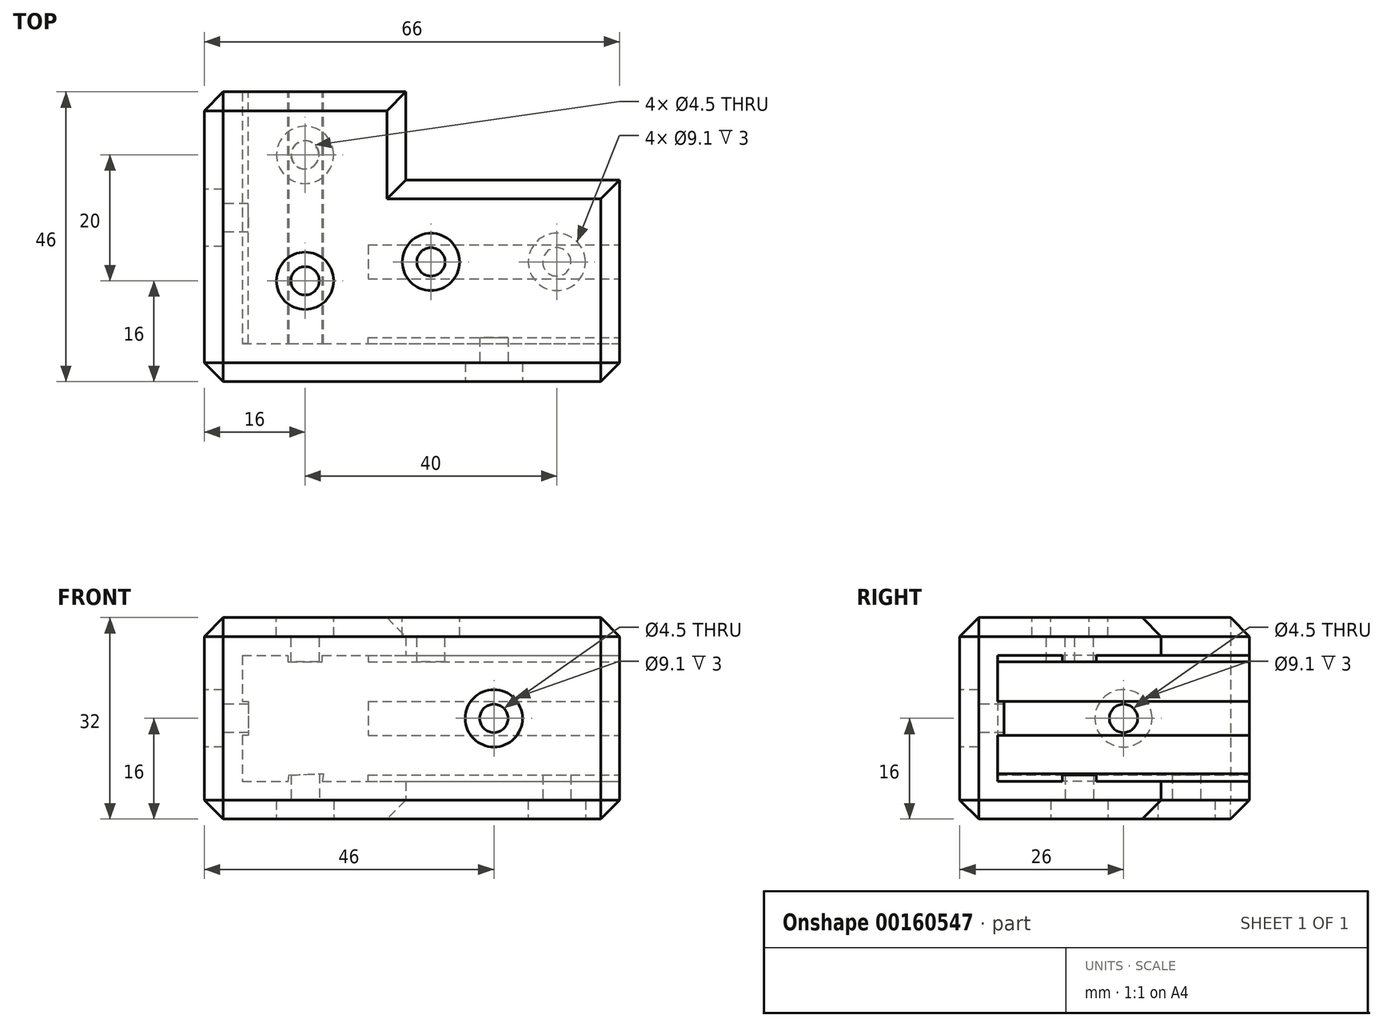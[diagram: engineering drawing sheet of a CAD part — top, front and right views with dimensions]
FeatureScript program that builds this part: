
annotation { "Feature Type Name" : "Feature", "Feature Type Description" : "" }
export const myFeature = defineFeature(function(context is Context, id is Id, definition is map)
    precondition{}
    {
        {
            var Q0;
            Q0=qCreatedBy(makeId("Top.planeOp"),FACE);
            var sketch = newSketch(context, id + "F0", { "sketchPlane" : qUnion([Q0])});
            skLineSegment(sketch, "E0", {"start": v(20, 40) * mm, "end": v(20, 20) * mm, "construction": true});
            skLineSegment(sketch, "E1", {"start": v(20, 20) * mm, "end": v(60, 20) * mm, "construction": true});
            skLineSegment(sketch, "E2", {"start": v(60, 20) * mm, "end": v(60, 0) * mm, "construction": true});
            skLineSegment(sketch, "E3", {"start": v(60, 0) * mm, "end": v(0, 0) * mm, "construction": true});
            skLineSegment(sketch, "E4", {"start": v(0, 0) * mm, "end": v(0, 40) * mm, "construction": true});
            skLineSegment(sketch, "E5", {"start": v(0, 40) * mm, "end": v(20, 40) * mm, "construction": true});
            skLineSegment(sketch, "E6", {"start": v(3.86, 40) * mm, "end": v(26, 40) * mm});
            skLineSegment(sketch, "E7", {"start": v(26, 40) * mm, "end": v(26, 26) * mm});
            skLineSegment(sketch, "E8", {"start": v(26, 26) * mm, "end": v(60, 26) * mm});
            skLineSegment(sketch, "E9", {"start": v(60, 26) * mm, "end": v(60, -6) * mm});
            skLineSegment(sketch, "E10", {"start": v(60, -6) * mm, "end": v(-6, -6) * mm});
            skLineSegment(sketch, "E11", {"start": v(-6, -6) * mm, "end": v(-6, 40) * mm});
            skLineSegment(sketch, "E12", {"start": v(-6, 40) * mm, "end": v(3.86, 40) * mm});
            skSolve(sketch);
        }
        {
            var Q0;
            Q0 = qSketchRegion(id + "F0", true);
            extrude(context, id + "F1", {"entities" : qUnion([Q0]), "depth" : 6 * mm});
        }
        {
            var Q0;
            Q0=makeQuery(id+"F1.opExtrude","CAP_FACE",FACE,{"disambiguationData":[OSD([sQuery(id+"F0.wireOp",EDGE,"E6"),sQuery(id+"F0.wireOp",EDGE,"E7"),sQuery(id+"F0.wireOp",EDGE,"E8"),sQuery(id+"F0.wireOp",EDGE,"E9"),sQuery(id+"F0.wireOp",EDGE,"E10"),sQuery(id+"F0.wireOp",EDGE,"E11"),sQuery(id+"F0.wireOp",EDGE,"E12")])],"isStart":false});
            var sketch = newSketch(context, id + "F2", { "sketchPlane" : qUnion([Q0])});
            skLineSegment(sketch, "E13", {"start": v(-6, 40) * mm, "end": v(0, 40) * mm});
            skLineSegment(sketch, "E14", {"start": v(0, 40) * mm, "end": v(0, 0) * mm});
            skLineSegment(sketch, "E15", {"start": v(0, 0) * mm, "end": v(60, 0) * mm});
            skLineSegment(sketch, "E16", {"start": v(60, 0) * mm, "end": v(60, -6) * mm});
            skLineSegment(sketch, "E17", {"start": v(60, -6) * mm, "end": v(-6, -6) * mm});
            skLineSegment(sketch, "E18", {"start": v(-6, -6) * mm, "end": v(-6, 40) * mm});
            skSolve(sketch);
        }
        {
            var Q0;
            Q0 = qSketchRegion(id + "F2", true);
            extrude(context, id + "F3", {"entities" : qUnion([Q0]), "operationType" : NewBodyOperationType.ADD, "depth" : 20 * mm});
        }
        {
            var Q0;
            Q0=makeQuery(id+"F3.opExtrude","CAP_FACE",FACE,{"disambiguationData":[OSD([sQuery(id+"F2.wireOp",EDGE,"E13"),sQuery(id+"F2.wireOp",EDGE,"E14"),sQuery(id+"F2.wireOp",EDGE,"E15"),sQuery(id+"F2.wireOp",EDGE,"E16"),sQuery(id+"F2.wireOp",EDGE,"E17"),sQuery(id+"F2.wireOp",EDGE,"E18")])],"isStart":false});
            var sketch = newSketch(context, id + "F4", { "sketchPlane" : qUnion([Q0])});
            skLineSegment(sketch, "E19", {"start": v(-6, -6) * mm, "end": v(-6, 40) * mm});
            skLineSegment(sketch, "E20", {"start": v(-6, 40) * mm, "end": v(26, 40) * mm});
            skLineSegment(sketch, "E21", {"start": v(26, 40) * mm, "end": v(26, 26) * mm});
            skLineSegment(sketch, "E22", {"start": v(26, 26) * mm, "end": v(60, 26) * mm});
            skLineSegment(sketch, "E23", {"start": v(60, 26) * mm, "end": v(60, -6) * mm});
            skLineSegment(sketch, "E24", {"start": v(60, -6) * mm, "end": v(-6, -6) * mm});
            skSolve(sketch);
        }
        {
            var Q0;
            Q0 = qSketchRegion(id + "F4", true);
            extrude(context, id + "F5", {"entities" : qUnion([Q0]), "operationType" : NewBodyOperationType.ADD, "depth" : 6 * mm});
        }
        {
            var Q0;
            Q0=makeQuery(id+"F5.boolean.opBoolean","MERGE",FACE,{"derivedFrom":[makeQuery(id+"F3.boolean.opBoolean","MERGE",FACE,{"derivedFrom":[makeQuery(id+"F1.opExtrude","SWEPT_FACE",FACE,{"disambiguationData":[OSD([sQuery(id+"F0.wireOp",EDGE,"E9")])]}),makeQuery(id+"F3.opExtrude","SWEPT_FACE",FACE,{"disambiguationData":[OSD([sQuery(id+"F2.wireOp",EDGE,"E16")])]})]}),makeQuery(id+"F5.opExtrude","SWEPT_FACE",FACE,{"disambiguationData":[OSD([sQuery(id+"F4.wireOp",EDGE,"E23")])]})]});
            var sketch = newSketch(context, id + "F6", { "sketchPlane" : qUnion([Q0])});
            skLineSegment(sketch, "E25", {"start": v(13, 26) * mm, "end": v(10.29, 26) * mm});
            skLineSegment(sketch, "E26", {"start": v(10.29, 26) * mm, "end": v(10.29, 25) * mm});
            skLineSegment(sketch, "E27", {"start": v(10.29, 25) * mm, "end": v(15.7, 25) * mm});
            skLineSegment(sketch, "E28", {"start": v(15.7, 25) * mm, "end": v(15.7, 26) * mm});
            skLineSegment(sketch, "E29", {"start": v(15.7, 26) * mm, "end": v(13, 26) * mm});
            skLineSegment(sketch, "E30", {"start": v(13, 6) * mm, "end": v(10.29, 6) * mm});
            skLineSegment(sketch, "E31", {"start": v(10.29, 6) * mm, "end": v(10.29, 7) * mm});
            skLineSegment(sketch, "E32", {"start": v(10.29, 7) * mm, "end": v(15.7, 7) * mm});
            skLineSegment(sketch, "E33", {"start": v(15.7, 7) * mm, "end": v(15.7, 6) * mm});
            skLineSegment(sketch, "E34", {"start": v(15.7, 6) * mm, "end": v(13, 6) * mm});
            skLineSegment(sketch, "E35", {"start": v(0, 16) * mm, "end": v(0, 18.7) * mm});
            skLineSegment(sketch, "E36", {"start": v(0, 18.7) * mm, "end": v(1, 18.7) * mm});
            skLineSegment(sketch, "E37", {"start": v(1, 18.7) * mm, "end": v(1, 13.29) * mm});
            skLineSegment(sketch, "E38", {"start": v(1, 13.29) * mm, "end": v(0, 13.29) * mm});
            skLineSegment(sketch, "E39", {"start": v(0, 13.29) * mm, "end": v(0, 16) * mm});
            skSolve(sketch);
        }
        {
            var Q0;
            Q0 = qSketchRegion(id + "F6", true);
            extrude(context, id + "F7", {"entities" : qUnion([Q0]), "operationType" : NewBodyOperationType.ADD, "oppositeDirection" : true, "depth" : 40 * mm});
        }
        {
            var Q0;
            Q0=makeQuery(id+"F5.boolean.opBoolean","MERGE",FACE,{"derivedFrom":[makeQuery(id+"F3.boolean.opBoolean","MERGE",FACE,{"derivedFrom":[makeQuery(id+"F1.opExtrude","SWEPT_FACE",FACE,{"disambiguationData":[OSD([sQuery(id+"F0.wireOp",EDGE,"E6"),sQuery(id+"F0.wireOp",EDGE,"E12")])]}),makeQuery(id+"F3.opExtrude","SWEPT_FACE",FACE,{"disambiguationData":[OSD([sQuery(id+"F2.wireOp",EDGE,"E13")])]})]}),makeQuery(id+"F5.opExtrude","SWEPT_FACE",FACE,{"disambiguationData":[OSD([sQuery(id+"F4.wireOp",EDGE,"E20")])]})]});
            var sketch = newSketch(context, id + "F8", { "sketchPlane" : qUnion([Q0])});
            skLineSegment(sketch, "E40", {"start": v(0, 16) * mm, "end": v(0, 18.71) * mm});
            skLineSegment(sketch, "E41", {"start": v(0, 18.71) * mm, "end": v(-1, 18.71) * mm});
            skLineSegment(sketch, "E42", {"start": v(-1, 18.7) * mm, "end": v(-1, 13.29) * mm});
            skLineSegment(sketch, "E43", {"start": v(-1, 13.29) * mm, "end": v(0, 13.29) * mm});
            skLineSegment(sketch, "E44", {"start": v(0, 13.29) * mm, "end": v(0, 16) * mm});
            skLineSegment(sketch, "E45", {"start": v(-10, 26) * mm, "end": v(-12.7, 26) * mm});
            skLineSegment(sketch, "E46", {"start": v(-7.3, 26) * mm, "end": v(-10, 26) * mm});
            skLineSegment(sketch, "E47", {"start": v(-10, 5.54) * mm, "end": v(-7.3, 6) * mm});
            skLineSegment(sketch, "E48", {"start": v(-7.3, 6) * mm, "end": v(-7.47, 6.99) * mm});
            skLineSegment(sketch, "E49", {"start": v(-7.47, 6.99) * mm, "end": v(-12.88, 7.2) * mm});
            skLineSegment(sketch, "E50", {"start": v(-12.88, 7.2) * mm, "end": v(-12.7, 6) * mm});
            skLineSegment(sketch, "E51", {"start": v(-12.7, 6) * mm, "end": v(-10, 5.54) * mm});
            skLineSegment(sketch, "E52", {"start": v(-7.3, 26) * mm, "end": v(-7.3, 25) * mm});
            skLineSegment(sketch, "E53", {"start": v(-7.3, 25) * mm, "end": v(-12.71, 25) * mm});
            skLineSegment(sketch, "E54", {"start": v(-12.71, 25) * mm, "end": v(-12.71, 26) * mm});
            skSolve(sketch);
        }
        {
            var Q0;
            Q0 = qSketchRegion(id + "F8", true);
            extrude(context, id + "F9", {"entities" : qUnion([Q0]), "operationType" : NewBodyOperationType.ADD, "oppositeDirection" : true, "depth" : 40 * mm});
        }
        {
            var Q0;
            Q0=makeQuery(id+"F1.opExtrude","CAP_FACE",FACE,{"disambiguationData":[OSD([sQuery(id+"F0.wireOp",EDGE,"E6"),sQuery(id+"F0.wireOp",EDGE,"E7"),sQuery(id+"F0.wireOp",EDGE,"E8"),sQuery(id+"F0.wireOp",EDGE,"E9"),sQuery(id+"F0.wireOp",EDGE,"E10"),sQuery(id+"F0.wireOp",EDGE,"E11"),sQuery(id+"F0.wireOp",EDGE,"E12")])],"isStart":true});
            var sketch = newSketch(context, id + "F10", { "sketchPlane" : qUnion([Q0])});
            skCircle(sketch, "E55", {"center": v(50, -13) * mm, "radius": 2.25 * mm});
            skCircle(sketch, "E56", {"center": v(10, -30) * mm, "radius": 2.25 * mm});
            skSolve(sketch);
        }
        {
            var Q0;
            Q0 = qSketchRegion(id + "F10", true);
            extrude(context, id + "F11", {"entities" : qUnion([Q0]), "operationType" : NewBodyOperationType.REMOVE, "endBound" : BoundingType.UP_TO_NEXT, "oppositeDirection" : true, "depth" : 25 * mm});
        }
        {
            var Q0;
            Q0=makeQuery(id+"F5.opExtrude","CAP_FACE",FACE,{"disambiguationData":[OSD([sQuery(id+"F4.wireOp",EDGE,"E19"),sQuery(id+"F4.wireOp",EDGE,"E20"),sQuery(id+"F4.wireOp",EDGE,"E21"),sQuery(id+"F4.wireOp",EDGE,"E22"),sQuery(id+"F4.wireOp",EDGE,"E23"),sQuery(id+"F4.wireOp",EDGE,"E24")])],"isStart":false});
            var sketch = newSketch(context, id + "F12", { "sketchPlane" : qUnion([Q0])});
            skCircle(sketch, "E57", {"center": v(10, 10) * mm, "radius": 2.25 * mm});
            skCircle(sketch, "E58", {"center": v(30, 13) * mm, "radius": 2.25 * mm});
            skSolve(sketch);
        }
        {
            var Q0;
            Q0 = qSketchRegion(id + "F12", true);
            extrude(context, id + "F13", {"entities" : qUnion([Q0]), "operationType" : NewBodyOperationType.REMOVE, "endBound" : BoundingType.UP_TO_NEXT, "oppositeDirection" : true, "depth" : 25 * mm});
        }
        {
            var Q0;
            Q0=makeQuery(id+"F5.boolean.opBoolean","MERGE",FACE,{"derivedFrom":[makeQuery(id+"F3.boolean.opBoolean","MERGE",FACE,{"derivedFrom":[makeQuery(id+"F1.opExtrude","SWEPT_FACE",FACE,{"disambiguationData":[OSD([sQuery(id+"F0.wireOp",EDGE,"E10")])]}),makeQuery(id+"F3.opExtrude","SWEPT_FACE",FACE,{"disambiguationData":[OSD([sQuery(id+"F2.wireOp",EDGE,"E17")])]})]}),makeQuery(id+"F5.opExtrude","SWEPT_FACE",FACE,{"disambiguationData":[OSD([sQuery(id+"F4.wireOp",EDGE,"E24")])]})]});
            var sketch = newSketch(context, id + "F14", { "sketchPlane" : qUnion([Q0])});
            skCircle(sketch, "E59", {"center": v(40, 16) * mm, "radius": 2.25 * mm});
            skSolve(sketch);
        }
        {
            var Q0;
            Q0 = qSketchRegion(id + "F14", true);
            extrude(context, id + "F15", {"entities" : qUnion([Q0]), "operationType" : NewBodyOperationType.REMOVE, "endBound" : BoundingType.UP_TO_NEXT, "oppositeDirection" : true, "depth" : 25 * mm});
        }
        {
            var Q0;
            Q0=makeQuery(id+"F5.boolean.opBoolean","MERGE",FACE,{"derivedFrom":[makeQuery(id+"F3.boolean.opBoolean","MERGE",FACE,{"derivedFrom":[makeQuery(id+"F1.opExtrude","SWEPT_FACE",FACE,{"disambiguationData":[OSD([sQuery(id+"F0.wireOp",EDGE,"E11")])]}),makeQuery(id+"F3.opExtrude","SWEPT_FACE",FACE,{"disambiguationData":[OSD([sQuery(id+"F2.wireOp",EDGE,"E18")])]})]}),makeQuery(id+"F5.opExtrude","SWEPT_FACE",FACE,{"disambiguationData":[OSD([sQuery(id+"F4.wireOp",EDGE,"E19")])]})]});
            var sketch = newSketch(context, id + "F16", { "sketchPlane" : qUnion([Q0])});
            skCircle(sketch, "E60", {"center": v(-20, 16) * mm, "radius": 2.25 * mm});
            skSolve(sketch);
        }
        {
            var Q0;
            Q0 = qSketchRegion(id + "F16", true);
            extrude(context, id + "F17", {"entities" : qUnion([Q0]), "operationType" : NewBodyOperationType.REMOVE, "endBound" : BoundingType.UP_TO_NEXT, "oppositeDirection" : true, "depth" : 25 * mm});
        }
        {
            var Q0;
            Q0=makeQuery(id+"F5.opExtrude","CAP_FACE",FACE,{"disambiguationData":[OSD([sQuery(id+"F4.wireOp",EDGE,"E19"),sQuery(id+"F4.wireOp",EDGE,"E20"),sQuery(id+"F4.wireOp",EDGE,"E21"),sQuery(id+"F4.wireOp",EDGE,"E22"),sQuery(id+"F4.wireOp",EDGE,"E23"),sQuery(id+"F4.wireOp",EDGE,"E24")])],"isStart":false});
            var sketch = newSketch(context, id + "F18", { "sketchPlane" : qUnion([Q0])});
            skCircle(sketch, "E61", {"center": v(10, 10) * mm, "radius": 4.55 * mm});
            skCircle(sketch, "E62", {"center": v(30, 13) * mm, "radius": 4.55 * mm});
            skSolve(sketch);
        }
        {
            var Q0;
            Q0 = qSketchRegion(id + "F18", true);
            extrude(context, id + "F19", {"entities" : qUnion([Q0]), "operationType" : NewBodyOperationType.REMOVE, "oppositeDirection" : true, "depth" : 3 * mm});
        }
        {
            var Q0;
            Q0=makeQuery(id+"F5.boolean.opBoolean","MERGE",FACE,{"derivedFrom":[makeQuery(id+"F3.boolean.opBoolean","MERGE",FACE,{"derivedFrom":[makeQuery(id+"F1.opExtrude","SWEPT_FACE",FACE,{"disambiguationData":[OSD([sQuery(id+"F0.wireOp",EDGE,"E11")])]}),makeQuery(id+"F3.opExtrude","SWEPT_FACE",FACE,{"disambiguationData":[OSD([sQuery(id+"F2.wireOp",EDGE,"E18")])]})]}),makeQuery(id+"F5.opExtrude","SWEPT_FACE",FACE,{"disambiguationData":[OSD([sQuery(id+"F4.wireOp",EDGE,"E19")])]})]});
            var sketch = newSketch(context, id + "F20", { "sketchPlane" : qUnion([Q0])});
            skCircle(sketch, "E63", {"center": v(-20, 16) * mm, "radius": 4.55 * mm});
            skSolve(sketch);
        }
        {
            var Q0;
            Q0 = qSketchRegion(id + "F20", true);
            extrude(context, id + "F21", {"entities" : qUnion([Q0]), "operationType" : NewBodyOperationType.REMOVE, "oppositeDirection" : true, "depth" : 3 * mm});
        }
        {
            var Q0;
            Q0=makeQuery(id+"F1.opExtrude","CAP_FACE",FACE,{"disambiguationData":[OSD([sQuery(id+"F0.wireOp",EDGE,"E6"),sQuery(id+"F0.wireOp",EDGE,"E7"),sQuery(id+"F0.wireOp",EDGE,"E8"),sQuery(id+"F0.wireOp",EDGE,"E9"),sQuery(id+"F0.wireOp",EDGE,"E10"),sQuery(id+"F0.wireOp",EDGE,"E11"),sQuery(id+"F0.wireOp",EDGE,"E12")])],"isStart":true});
            var sketch = newSketch(context, id + "F22", { "sketchPlane" : qUnion([Q0])});
            skCircle(sketch, "E64", {"center": v(10, -30) * mm, "radius": 4.55 * mm});
            skCircle(sketch, "E65", {"center": v(50, -13) * mm, "radius": 4.55 * mm});
            skSolve(sketch);
        }
        {
            var Q0;
            Q0 = qSketchRegion(id + "F22", true);
            extrude(context, id + "F23", {"entities" : qUnion([Q0]), "operationType" : NewBodyOperationType.REMOVE, "oppositeDirection" : true, "depth" : 3 * mm});
        }
        {
            var Q0;
            Q0=makeQuery(id+"F5.boolean.opBoolean","MERGE",FACE,{"derivedFrom":[makeQuery(id+"F3.boolean.opBoolean","MERGE",FACE,{"derivedFrom":[makeQuery(id+"F1.opExtrude","SWEPT_FACE",FACE,{"disambiguationData":[OSD([sQuery(id+"F0.wireOp",EDGE,"E10")])]}),makeQuery(id+"F3.opExtrude","SWEPT_FACE",FACE,{"disambiguationData":[OSD([sQuery(id+"F2.wireOp",EDGE,"E17")])]})]}),makeQuery(id+"F5.opExtrude","SWEPT_FACE",FACE,{"disambiguationData":[OSD([sQuery(id+"F4.wireOp",EDGE,"E24")])]})]});
            var sketch = newSketch(context, id + "F24", { "sketchPlane" : qUnion([Q0])});
            skCircle(sketch, "E66", {"center": v(40, 16) * mm, "radius": 4.55 * mm});
            skSolve(sketch);
        }
        {
            var Q0;
            Q0 = qSketchRegion(id + "F24", true);
            extrude(context, id + "F25", {"entities" : qUnion([Q0]), "operationType" : NewBodyOperationType.REMOVE, "oppositeDirection" : true, "depth" : 3 * mm});
        }
        {
            var Q0;
            Q0=makeQuery(id+"F1.opExtrude","CAP_EDGE",EDGE,{"disambiguationData":[OSD([sQuery(id+"F0.wireOp",EDGE,"E10")])],"isStart":true});
            var Q1;
            Q1=makeQuery(id+"F1.opExtrude","CAP_EDGE",EDGE,{"disambiguationData":[OSD([sQuery(id+"F0.wireOp",EDGE,"E8")])],"isStart":true});
            var Q2;
            Q2=makeQuery(id+"F1.opExtrude","CAP_EDGE",EDGE,{"disambiguationData":[OSD([sQuery(id+"F0.wireOp",EDGE,"E7")])],"isStart":true});
            var Q3;
            Q3=makeQuery(id+"F1.opExtrude","CAP_EDGE",EDGE,{"disambiguationData":[OSD([sQuery(id+"F0.wireOp",EDGE,"E6"),sQuery(id+"F0.wireOp",EDGE,"E12")])],"isStart":true});
            var Q4;
            Q4=makeQuery(id+"F1.opExtrude","CAP_EDGE",EDGE,{"disambiguationData":[OSD([sQuery(id+"F0.wireOp",EDGE,"E11")])],"isStart":true});
            var Q5;
            Q5=makeQuery(id+"F5.boolean.opBoolean","MERGE",EDGE,{"derivedFrom":[makeQuery(id+"F3.boolean.opBoolean","MERGE",EDGE,{"derivedFrom":[makeQuery(id+"F1.opExtrude","SWEPT_EDGE",EDGE,{"disambiguationData":[OSD([sQuery(id+"F0.wireOp",EDGE,"E10"),sQuery(id+"F0.wireOp",EDGE,"E11")])]}),makeQuery(id+"F3.opExtrude","SWEPT_EDGE",EDGE,{"disambiguationData":[OSD([sQuery(id+"F2.wireOp",EDGE,"E17"),sQuery(id+"F2.wireOp",EDGE,"E18")])]})]}),makeQuery(id+"F5.opExtrude","SWEPT_EDGE",EDGE,{"disambiguationData":[OSD([sQuery(id+"F4.wireOp",EDGE,"E19"),sQuery(id+"F4.wireOp",EDGE,"E24")])]})]});
            var Q6;
            Q6=makeQuery(id+"F5.opExtrude","CAP_EDGE",EDGE,{"disambiguationData":[OSD([sQuery(id+"F4.wireOp",EDGE,"E24")])],"isStart":false});
            var Q7;
            Q7=makeQuery(id+"F5.opExtrude","CAP_EDGE",EDGE,{"disambiguationData":[OSD([sQuery(id+"F4.wireOp",EDGE,"E19")])],"isStart":false});
            var Q8;
            Q8=makeQuery(id+"F5.opExtrude","CAP_EDGE",EDGE,{"disambiguationData":[OSD([sQuery(id+"F4.wireOp",EDGE,"E20")])],"isStart":false});
            var Q9;
            Q9=makeQuery(id+"F5.opExtrude","CAP_EDGE",EDGE,{"disambiguationData":[OSD([sQuery(id+"F4.wireOp",EDGE,"E21")])],"isStart":false});
            var Q10;
            Q10=makeQuery(id+"F5.opExtrude","CAP_EDGE",EDGE,{"disambiguationData":[OSD([sQuery(id+"F4.wireOp",EDGE,"E22")])],"isStart":false});
            var Q11;
            Q11=makeQuery(id+"F5.opExtrude","CAP_EDGE",EDGE,{"disambiguationData":[OSD([sQuery(id+"F4.wireOp",EDGE,"E23")])],"isStart":false});
            var Q12;
            Q12=makeQuery(id+"F1.opExtrude","CAP_EDGE",EDGE,{"disambiguationData":[OSD([sQuery(id+"F0.wireOp",EDGE,"E9")])],"isStart":true});
            var Q13;
            Q13=makeQuery(id+"F5.boolean.opBoolean","MERGE",EDGE,{"derivedFrom":[makeQuery(id+"F3.boolean.opBoolean","MERGE",EDGE,{"derivedFrom":[makeQuery(id+"F1.opExtrude","SWEPT_EDGE",EDGE,{"disambiguationData":[OSD([sQuery(id+"F0.wireOp",EDGE,"E11"),sQuery(id+"F0.wireOp",EDGE,"E12")])]}),makeQuery(id+"F3.opExtrude","SWEPT_EDGE",EDGE,{"disambiguationData":[OSD([sQuery(id+"F2.wireOp",EDGE,"E13"),sQuery(id+"F2.wireOp",EDGE,"E18")])]})]}),makeQuery(id+"F5.opExtrude","SWEPT_EDGE",EDGE,{"disambiguationData":[OSD([sQuery(id+"F4.wireOp",EDGE,"E19"),sQuery(id+"F4.wireOp",EDGE,"E20")])]})]});
            var Q14;
            Q14=makeQuery(id+"F5.boolean.opBoolean","MERGE",EDGE,{"derivedFrom":[makeQuery(id+"F3.boolean.opBoolean","MERGE",EDGE,{"derivedFrom":[makeQuery(id+"F1.opExtrude","SWEPT_EDGE",EDGE,{"disambiguationData":[OSD([sQuery(id+"F0.wireOp",EDGE,"E9"),sQuery(id+"F0.wireOp",EDGE,"E10")])]}),makeQuery(id+"F3.opExtrude","SWEPT_EDGE",EDGE,{"disambiguationData":[OSD([sQuery(id+"F2.wireOp",EDGE,"E16"),sQuery(id+"F2.wireOp",EDGE,"E17")])]})]}),makeQuery(id+"F5.opExtrude","SWEPT_EDGE",EDGE,{"disambiguationData":[OSD([sQuery(id+"F4.wireOp",EDGE,"E23"),sQuery(id+"F4.wireOp",EDGE,"E24")])]})]});
            chamfer(context, id + "F26", {"entities" : qUnion([Q0, Q1, Q2, Q3, Q4, Q5, Q6, Q7, Q8, Q9, Q10, Q11, Q12, Q13, Q14]), "width" : 3 * mm, "tangentPropagation" : true});
        }
    });
